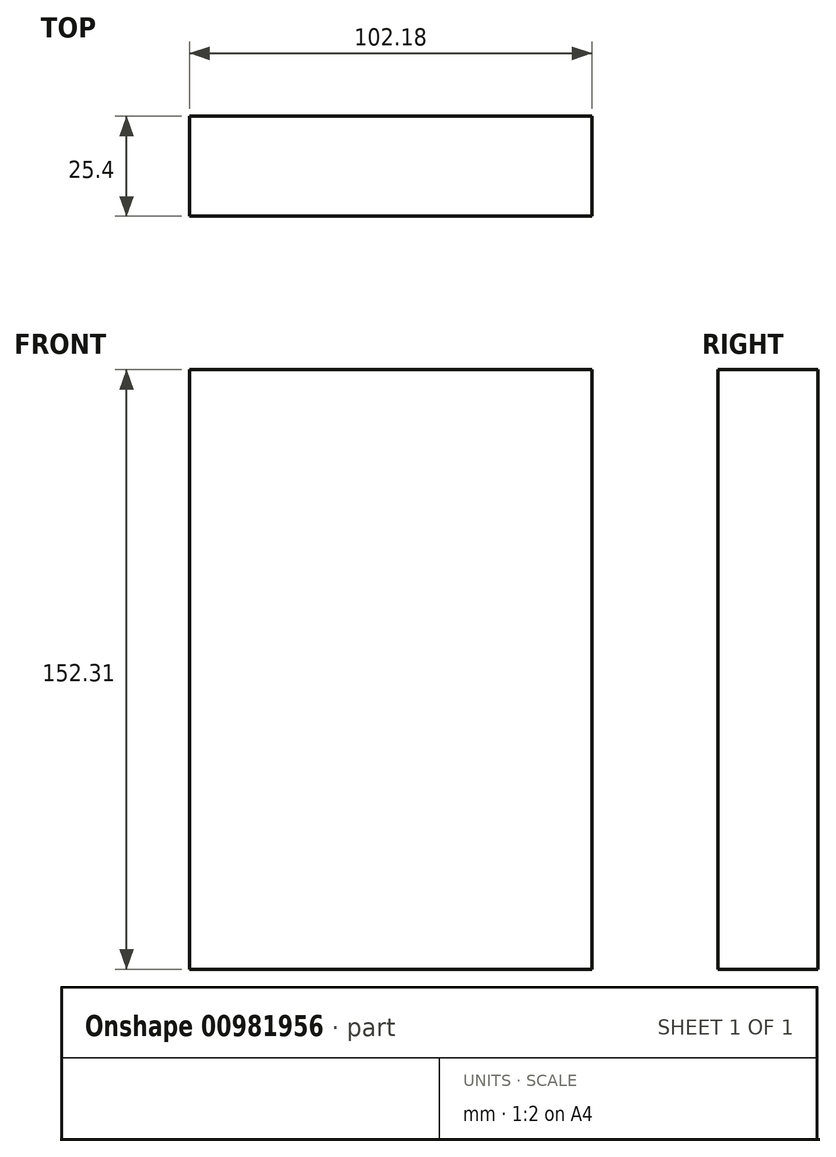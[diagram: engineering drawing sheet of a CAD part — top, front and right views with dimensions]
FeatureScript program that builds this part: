
annotation { "Feature Type Name" : "Feature", "Feature Type Description" : "" }
export const myFeature = defineFeature(function(context is Context, id is Id, definition is map)
    precondition{}
    {
        {
            var Q0;
            Q0=qCreatedBy(makeId("Front.planeOp"),FACE);
            var sketch = newSketch(context, id + "F0", { "sketchPlane" : qUnion([Q0])});
            skLineSegment(sketch, "E0.bottom", {"start": v(-51.67, 76.35) * mm, "end": v(50.51, 76.35) * mm});
            skLineSegment(sketch, "E0.top", {"start": v(-51.67, -75.96) * mm, "end": v(50.51, -75.96) * mm});
            skLineSegment(sketch, "E0.left", {"start": v(-51.67, 76.35) * mm, "end": v(-51.67, -75.96) * mm});
            skLineSegment(sketch, "E0.right", {"start": v(50.51, 76.35) * mm, "end": v(50.51, -75.96) * mm});
            skSolve(sketch);
        }
        {
            var Q0;
            Q0=makeQuery(id+"F0.imprint","IMPRINT",FACE,{"disambiguationData":[TD([[makeQuery(id+"F0.imprint","IMPRINT",EDGE,{"derivedFrom":sQuery(id+"F0.wireOp",EDGE,"E0.bottom")}),-1.0]])]});
            extrude(context, id + "F1", {"entities" : qUnion([Q0]), "depth" : 25.4 * mm, "offsetDistance" : 25.4 * mm});
        }
    });
